# Revit family: Haworth_Planes_DiscussionTable_AP_PRELIMINARY
name_source: partatom
category: Furniture
units: mm (PartAtom-declared; Revit-internal decimal feet)

## family parameters
Always vertical = Yes
Cut with Voids When Loaded = No
OmniClass Number = 23.40.70.14.64.21
OmniClass Title = Systems Furniture
Room Calculation Point = No
Shared = No
Work Plane-Based = No

## types (3) — shared parameters
Actual Height = 740 mm  [stored 2.42782 ft]
Assembly Code = E2020200
Description = Haworth - Planes - Discussion Table
Flip Top Finish = Haworth _ Paint _ Undecided _ Table
Glide Finish = Haworth _ Polymer _ Black
Leg Height = 710 mm
Manufacturer = Haworth
Model = WOPLTD
Revision Number = 1
Size = Verify Final Dim. w/ Haworth
URL = https://www.haworth.com
URL - Product = https://www.haworth.com
Warranty = http://www.haworth.com

## per-type parameters (varying)
| type | Actual Depth | Actual Diameter | Actual Width | Casters | Cutout | Glides | Large | Medium | Small | with Cutout |
| 850dia | 850 mm  [stored 2.78871 ft] | 425 mm  [stored 1.39436 ft] | 850 mm  [stored 2.78871 ft] | No | No | Yes | No | No | Yes | 690 mm  [stored 2.26378 ft] |
| 900dia | 900 mm  [stored 2.95276 ft] | 450 mm  [stored 1.47638 ft] | 900 mm  [stored 2.95276 ft] | No | Yes | Yes | No | Yes | No | 770 mm  [stored 2.52625 ft] |
| 1000dia | 1000 mm  [stored 3.28084 ft] | 500 mm  [stored 1.64042 ft] | 1000 mm  [stored 3.28084 ft] | Yes | Yes | No | Yes | No | No | 770 mm  [stored 2.52625 ft] |

note: [stored X ft] marks values corroborated as IEEE doubles in the binary element streams (Revit-internal decimal feet)

## geometry (parser evidence)
native form markers: Sweep x8
no freeform markers — native parametric forms only
